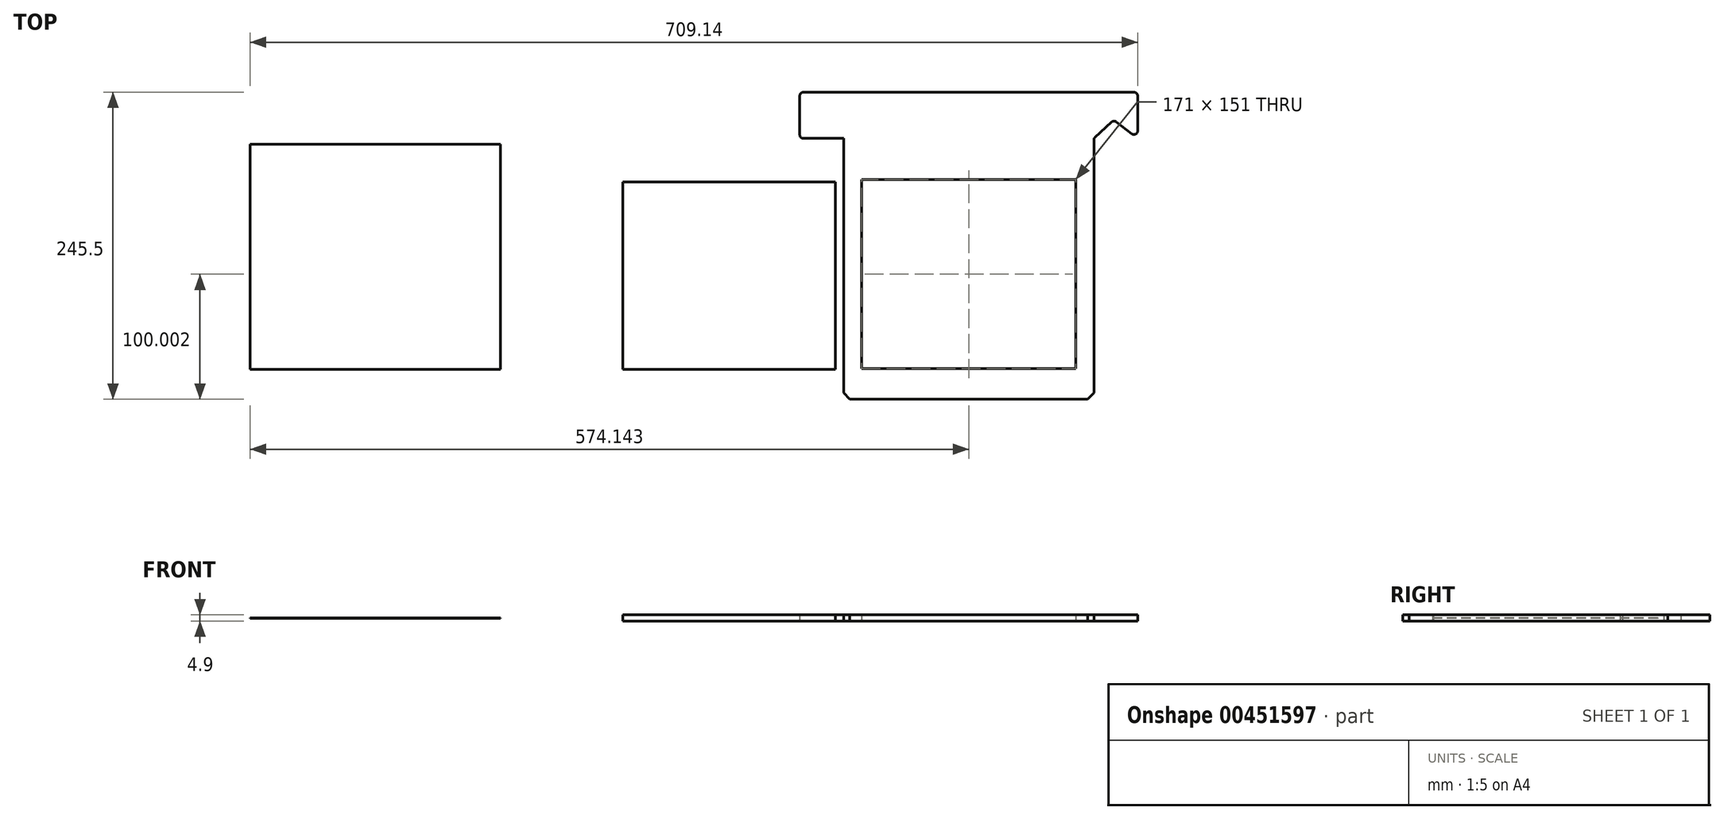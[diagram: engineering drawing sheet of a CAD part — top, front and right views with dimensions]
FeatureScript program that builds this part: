
annotation { "Feature Type Name" : "Feature", "Feature Type Description" : "" }
export const myFeature = defineFeature(function(context is Context, id is Id, definition is map)
    precondition{}
    {
        {
            var Q0;
            Q0=qCreatedBy(makeId("Top.planeOp"),FACE);
            var sketch = newSketch(context, id + "F0", { "sketchPlane" : qUnion([Q0])});
            skLineSegment(sketch, "E0", {"start": v(-61.24, -165.7) * mm, "end": v(138.76, -165.7) * mm});
            skLineSegment(sketch, "E1", {"start": v(-61.24, -165.7) * mm, "end": v(-61.24, 42.8) * mm});
            skLineSegment(sketch, "E2", {"start": v(-61.24, 42.8) * mm, "end": v(-96.24, 42.8) * mm});
            skLineSegment(sketch, "E3", {"start": v(-96.24, 42.8) * mm, "end": v(-96.24, 79.8) * mm});
            skLineSegment(sketch, "E4", {"start": v(-96.24, 79.8) * mm, "end": v(173.76, 79.8) * mm});
            skLineSegment(sketch, "E5", {"start": v(173.76, 79.8) * mm, "end": v(173.76, 42.8) * mm});
            skLineSegment(sketch, "E6", {"start": v(138.76, -165.7) * mm, "end": v(138.76, 42.8) * mm});
            skLineSegment(sketch, "E7", {"start": v(138.76, 42.8) * mm, "end": v(154.76, 57.63) * mm});
            skLineSegment(sketch, "E8", {"start": v(154.76, 57.63) * mm, "end": v(173.76, 42.8) * mm});
            skLineSegment(sketch, "E9.bottom", {"start": v(-46.74, 9.8) * mm, "end": v(124.26, 9.8) * mm});
            skLineSegment(sketch, "E9.top", {"start": v(-46.74, -141.2) * mm, "end": v(124.26, -141.2) * mm});
            skLineSegment(sketch, "E9.left", {"start": v(-46.74, 9.8) * mm, "end": v(-46.74, -141.2) * mm});
            skLineSegment(sketch, "E9.right", {"start": v(124.26, 9.8) * mm, "end": v(124.26, -141.2) * mm});
            skPoint(sketch, "E10", {"position": v(154.76, 57.63) * mm});
            skSolve(sketch);
        }
        {
            var Q0;
            Q0=makeQuery(id+"F0.imprint","IMPRINT",FACE,{"disambiguationData":[TD([[makeQuery(id+"F0.imprint","IMPRINT",EDGE,{"derivedFrom":sQuery(id+"F0.wireOp",EDGE,"E0")}),1.0]])]});
            extrude(context, id + "F1", {"entities" : qUnion([Q0]), "endBound" : BoundingType.SYMMETRIC, "depth" : 4.9 * mm});
        }
        {
            var Q0;
            Q0=makeQuery(id+"F1.opExtrude","SWEPT_EDGE",EDGE,{"disambiguationData":[OSD([sQuery(id+"F0.wireOp",EDGE,"E3"),sQuery(id+"F0.wireOp",EDGE,"E4")])]});
            var Q1;
            Q1=makeQuery(id+"F1.opExtrude","SWEPT_EDGE",EDGE,{"disambiguationData":[OSD([sQuery(id+"F0.wireOp",EDGE,"E4"),sQuery(id+"F0.wireOp",EDGE,"E5")])]});
            var Q2;
            Q2=makeQuery(id+"F1.opExtrude","SWEPT_EDGE",EDGE,{"disambiguationData":[OSD([sQuery(id+"F0.wireOp",EDGE,"E5"),sQuery(id+"F0.wireOp",EDGE,"E8")])]});
            var Q3;
            Q3=makeQuery(id+"F1.opExtrude","SWEPT_EDGE",EDGE,{"disambiguationData":[OSD([sQuery(id+"F0.wireOp",EDGE,"E6"),sQuery(id+"F0.wireOp",EDGE,"E7")])]});
            var Q4;
            Q4=makeQuery(id+"F1.opExtrude","SWEPT_EDGE",EDGE,{"disambiguationData":[OSD([sQuery(id+"F0.wireOp",EDGE,"E7"),sQuery(id+"F0.wireOp",EDGE,"E8")])]});
            fillet(context, id + "F2", {"entities" : qUnion([Q0, Q1, Q2, Q3, Q4]), "radius" : 3 * mm, "tangentPropagation" : true, "allowEdgeOverflow" : false});
        }
        {
            var Q0;
            Q0=makeQuery(id+"F1.opExtrude","SWEPT_EDGE",EDGE,{"disambiguationData":[OSD([sQuery(id+"F0.wireOp",EDGE,"E2"),sQuery(id+"F0.wireOp",EDGE,"E3")])]});
            fillet(context, id + "F3", {"entities" : qUnion([Q0]), "radius" : 3 * mm, "tangentPropagation" : true, "allowEdgeOverflow" : false});
        }
        {
            var Q0;
            Q0=makeQuery(id+"F1.opExtrude","SWEPT_EDGE",EDGE,{"disambiguationData":[OSD([sQuery(id+"F0.wireOp",EDGE,"E0"),sQuery(id+"F0.wireOp",EDGE,"E1")])]});
            var Q1;
            Q1=makeQuery(id+"F1.opExtrude","SWEPT_EDGE",EDGE,{"disambiguationData":[OSD([sQuery(id+"F0.wireOp",EDGE,"E0"),sQuery(id+"F0.wireOp",EDGE,"E6")])]});
            chamfer(context, id + "F4", {"entities" : qUnion([Q0, Q1]), "width" : 5 * mm, "tangentPropagation" : true});
        }
        {
            var Q0;
            Q0=qCreatedBy(makeId("Top.planeOp"),FACE);
            var sketch = newSketch(context, id + "F5", { "sketchPlane" : qUnion([Q0])});
            skLineSegment(sketch, "E11.bottom", {"start": v(-237.75, 8.04) * mm, "end": v(-67.75, 8.04) * mm});
            skLineSegment(sketch, "E11.top", {"start": v(-237.75, -141.96) * mm, "end": v(-67.75, -141.96) * mm});
            skLineSegment(sketch, "E11.left", {"start": v(-237.75, 8.04) * mm, "end": v(-237.75, -141.96) * mm});
            skLineSegment(sketch, "E11.right", {"start": v(-67.75, 8.04) * mm, "end": v(-67.75, -141.96) * mm});
            skSolve(sketch);
        }
        {
            var Q0;
            Q0=makeQuery(id+"F5.imprint","IMPRINT",FACE,{"disambiguationData":[TD([[makeQuery(id+"F5.imprint","IMPRINT",EDGE,{"derivedFrom":sQuery(id+"F5.wireOp",EDGE,"E11.bottom")}),-1.0]])]});
            extrude(context, id + "F6", {"entities" : qUnion([Q0]), "endBound" : BoundingType.SYMMETRIC, "depth" : 4.9 * mm});
        }
        {
            var Q0;
            Q0=qCreatedBy(makeId("Top.planeOp"),FACE);
            var sketch = newSketch(context, id + "F7", { "sketchPlane" : qUnion([Q0])});
            skLineSegment(sketch, "E12.bottom", {"start": v(-535.38, 38.07) * mm, "end": v(-335.38, 38.07) * mm});
            skLineSegment(sketch, "E12.top", {"start": v(-535.38, -141.93) * mm, "end": v(-335.38, -141.93) * mm});
            skLineSegment(sketch, "E12.left", {"start": v(-535.38, 38.07) * mm, "end": v(-535.38, -141.93) * mm});
            skLineSegment(sketch, "E12.right", {"start": v(-335.38, 38.07) * mm, "end": v(-335.38, -141.93) * mm});
            skSolve(sketch);
        }
        {
            var Q0;
            Q0=makeQuery(id+"F7.imprint","IMPRINT",FACE,{"disambiguationData":[TD([[makeQuery(id+"F7.imprint","IMPRINT",EDGE,{"derivedFrom":sQuery(id+"F7.wireOp",EDGE,"E12.bottom")}),-1.0]])]});
            extrude(context, id + "F8", {"entities" : qUnion([Q0]), "endBound" : BoundingType.SYMMETRIC, "depth" : 0.3 * mm});
        }
    });
